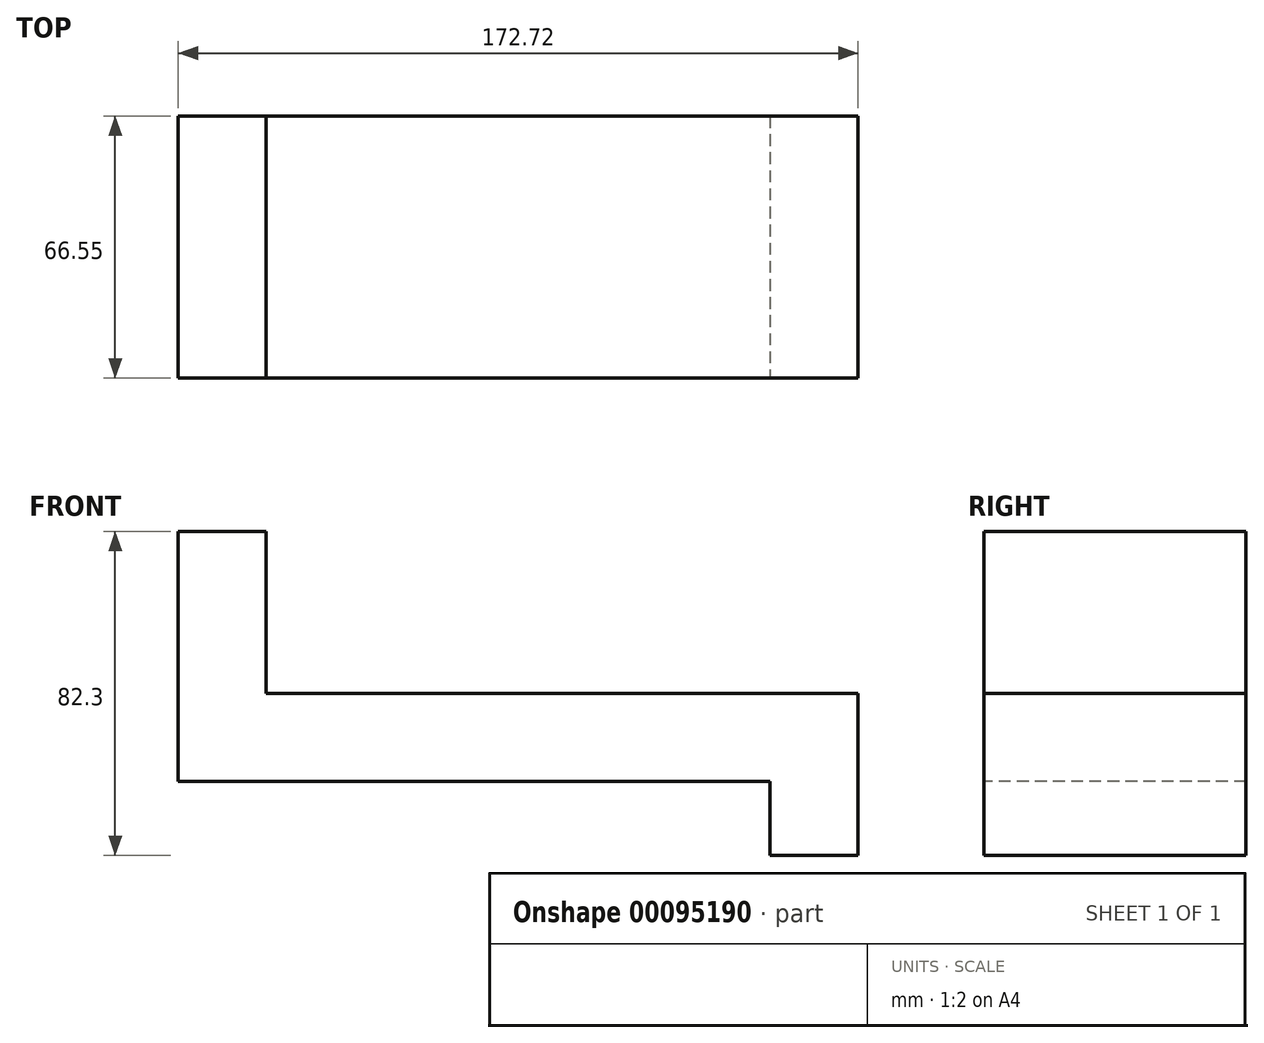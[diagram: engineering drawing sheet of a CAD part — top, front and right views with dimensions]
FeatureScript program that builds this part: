
annotation { "Feature Type Name" : "Feature", "Feature Type Description" : "" }
export const myFeature = defineFeature(function(context is Context, id is Id, definition is map)
    precondition{}
    {
        {
            var Q0;
            Q0=qCreatedBy(makeId("Front.planeOp"),FACE);
            var sketch = newSketch(context, id + "F0", { "sketchPlane" : qUnion([Q0])});
            skLineSegment(sketch, "E0.bottom", {"start": v(-66.62, 16.79) * mm, "end": v(-44.27, 16.79) * mm});
            skLineSegment(sketch, "E0.top", {"start": v(-66.62, -46.71) * mm, "end": v(-44.27, -46.71) * mm});
            skLineSegment(sketch, "E0.left", {"start": v(-66.62, 16.79) * mm, "end": v(-66.62, -46.71) * mm});
            skLineSegment(sketch, "E0.right", {"start": v(-44.27, 16.79) * mm, "end": v(-44.27, -46.71) * mm});
            skLineSegment(sketch, "E1.bottom", {"start": v(-44.27, -46.71) * mm, "end": v(83.75, -46.71) * mm});
            skLineSegment(sketch, "E1.top", {"start": v(-44.27, -24.36) * mm, "end": v(83.75, -24.36) * mm});
            skLineSegment(sketch, "E1.left", {"start": v(-44.27, -46.71) * mm, "end": v(-44.27, -24.36) * mm});
            skLineSegment(sketch, "E1.right", {"start": v(83.75, -46.71) * mm, "end": v(83.75, -24.36) * mm});
            skLineSegment(sketch, "E2.bottom", {"start": v(83.75, -24.36) * mm, "end": v(106.1, -24.36) * mm});
            skLineSegment(sketch, "E2.top", {"start": v(83.75, -65.5) * mm, "end": v(106.1, -65.5) * mm});
            skLineSegment(sketch, "E2.left", {"start": v(83.75, -24.36) * mm, "end": v(83.75, -65.5) * mm});
            skLineSegment(sketch, "E2.right", {"start": v(106.1, -24.36) * mm, "end": v(106.1, -65.5) * mm});
            skSolve(sketch);
        }
        {
            var Q0;
            Q0 = qSketchRegion(id + "F0", true);
            extrude(context, id + "F1", {"entities" : qUnion([Q0]), "oppositeDirection" : true, "depth" : 66.55 * mm});
        }
    });
